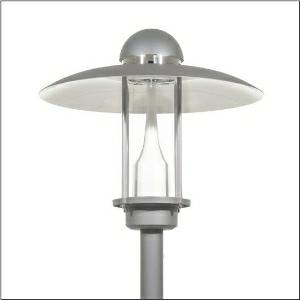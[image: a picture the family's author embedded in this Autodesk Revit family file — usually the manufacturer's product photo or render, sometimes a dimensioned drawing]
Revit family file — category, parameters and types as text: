
# Revit family: city-light_elegance_iq___p1_0a_5xa5265nf14h_5982
name_source: partatom
category: Lighting Fixtures
units: mm (PartAtom-declared; Revit-internal decimal feet)

## family parameters
Cut with Voids When Loaded = No
Host = Face
Light Source = No
Part Type = Normal
Room Calculation Point = No
Round Connector Dimension = Use Diameter
Shared = No

## types (1)
- --- (1 x LED, 1440 lm, 11.8 W, 2700K)
    Apparent Load = 12 VA
    CIE Flux Codes = 32 62 91 97 100
    Color Rendering = 70
    Color Temperature = 2700K
    Default Elevation = 1800 mm
    Description = City-Light Elegance iQ, mast luminaire, Module 540 iQ-SR, primary light control with 3 zone facetted reflector, of plastic, silver coated, highly specular, structured, primary optical cover: cover, of PMMA, transparent, light distribution: P1.0a, light emission: direct distribution, primary light characteristic: strongly asymmetric, installation type: post-top, LED, High Power LED, rated luminous flux: 1.440lm, luminous efficacy: 122lm/W, light colour: 727, colour temperature: 2700K, control gear: iQ Street-Remote, control: pre-setting: logarithmic dimming characteristic, Street-Remote, Auto-Match, Temp-Guard, Lumen-Switch, Night-Set, Smart-Wire, Light-Fading, Desk-Remote (wireless, voltage-free reading and setting of iQ features in the workshop via application-optimized NFC function/RFID function), optimised constant luminous flux control (CLO 2.0), with terminal, 6-pole, max. 2.5mm², mains connection: 230..240V, AC, 50/60Hz, start of lifetime: 12W, end of service life: 12W, reduction: 6W, luminaire housing, upper part, of aluminium, coated, Siteco® metallic grey (DB 702S), diameter: 750mm, height: 675mm, spigot size: d x l = 76 x 70mm (post-top) | with reducer (optional accessory) 60 x 70mm, mounting height: 3..5m, post-top mast mounting element, of diecast aluminium, coated, Siteco® metallic grey (DB 702S), Module 540 iQ-SR, traffic white (RAL 9016), equipment: standard, protection rating (complete): IP65, insulation class (complete): insulation class II (safety insulation), certification: CE, ENEC, VDE, packaging unit: 1 piece

Light Distribution: P1.0a
    Height = 675 mm
    Lamp = 1 x LED
    Lamp Light Flux = 1440 lm
    Lamp Power = 11.8 W
    Lamp count = 1
    Length = 750 mm
    Luminous efficacy = 122 lm/W
    Manufacturer = Siteco
    ModVariant = No
    Model = 5XA5265NF14H
    Number of Poles = 1
    OnlyDefault = Yes
    Power Factor = 1
    Product Name = City-Light Elegance iQ | P1.0a
    Product group = mast luminaire | pylon top
    ProductGroupID = 6100
    Protection Class = Protection class II
    Protection Degree = IP 65
    RLX_Detail_Level = 1
    RLX_Emergency_Light_Flux = 0 lm
    RLX_Emergency_Type = 0
    RLX_Emergency_Type_DB = No
    RlxData = <blob elided: 62577 chars, md5=ccd03fdf>
    Socket = socket
    Standby Power = 0 W
    System Light Flux = 1440 lm
    System Power = 12 W
    Type Comments = factory setting: luminous flux: 100 % | dim-lin: 254 | 472 mA
    Type Image = l_1006912.jpg
    URL = http://relux.com
    VarID = @adj_153254
    Voltage = 0 V
    Weight = 0.00 kg
    Width = 0 mm  [stored 0 ft]

note: [stored X ft] marks values corroborated as IEEE doubles in the binary element streams (Revit-internal decimal feet)

## geometry (parser evidence)
native form markers: Blend x4, Sweep x10
no freeform markers — native parametric forms only
